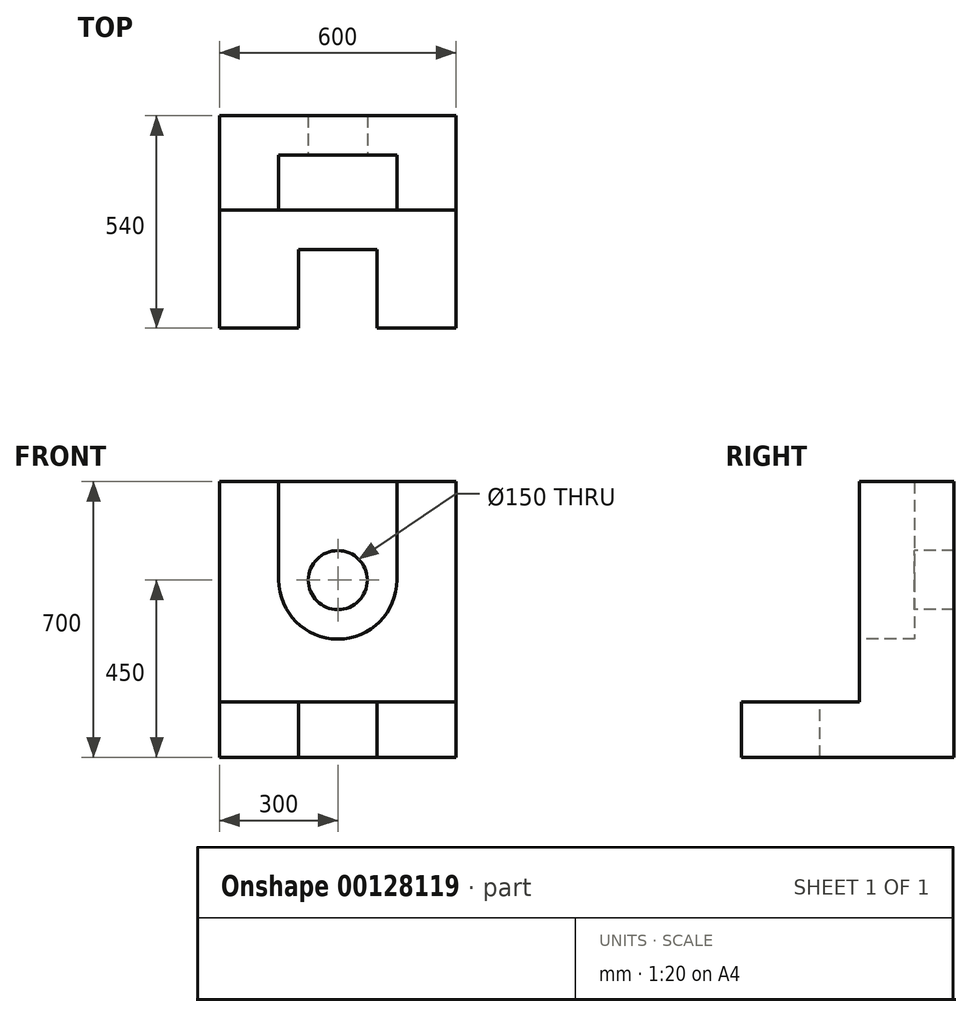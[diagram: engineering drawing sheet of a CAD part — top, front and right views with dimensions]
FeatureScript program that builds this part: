
annotation { "Feature Type Name" : "Feature", "Feature Type Description" : "" }
export const myFeature = defineFeature(function(context is Context, id is Id, definition is map)
    precondition{}
    {
        {
            var Q0;
            Q0=qCreatedBy(makeId("Top.planeOp"),FACE);
            var sketch = newSketch(context, id + "F0", { "sketchPlane" : qUnion([Q0])});
            skLineSegment(sketch, "E0.bottom", {"start": v(300, -150) * mm, "end": v(-300, -150) * mm});
            skLineSegment(sketch, "E0.top", {"start": v(300, 150) * mm, "end": v(-300, 150) * mm});
            skLineSegment(sketch, "E0.left", {"start": v(300, -150) * mm, "end": v(300, 150) * mm});
            skLineSegment(sketch, "E0.right", {"start": v(-300, -150) * mm, "end": v(-300, 150) * mm});
            skPoint(sketch, "E0.middle", {"position": v(0, 0) * mm});
            skSolve(sketch);
        }
        {
            var Q0;
            Q0 = qSketchRegion(id + "F0", true);
            extrude(context, id + "F1", {"entities" : qUnion([Q0]), "depth" : 140 * mm});
        }
        {
            var Q0;
            Q0=makeQuery(id+"F1.opExtrude","CAP_FACE",FACE,{"disambiguationData":[OSD([sQuery(id+"F0.wireOp",EDGE,"E0.bottom"),sQuery(id+"F0.wireOp",EDGE,"E0.top"),sQuery(id+"F0.wireOp",EDGE,"E0.left"),sQuery(id+"F0.wireOp",EDGE,"E0.right")])],"isStart":false});
            var sketch = newSketch(context, id + "F2", { "sketchPlane" : qUnion([Q0])});
            skLineSegment(sketch, "E1.bottom", {"start": v(100, 50) * mm, "end": v(-100, 50) * mm});
            skLineSegment(sketch, "E1.top", {"start": v(100, -350) * mm, "end": v(-100, -350) * mm});
            skLineSegment(sketch, "E1.left", {"start": v(100, 50) * mm, "end": v(100, -350) * mm});
            skLineSegment(sketch, "E1.right", {"start": v(-100, 50) * mm, "end": v(-100, -350) * mm});
            skPoint(sketch, "E1.middle", {"position": v(0, -150) * mm});
            skSolve(sketch);
        }
        {
            var Q0;
            {var subQ0=sQuery(id+"F2.wireOp",EDGE,"E1.bottom");Q0=makeQuery(id+"F2.imprint","IMPRINT",FACE,{"disambiguationData":[TD([[makeQuery(id+"F2.imprint","IMPRINT",EDGE,{"derivedFrom":subQ0}),1.0]])]});}
            extrude(context, id + "F3", {"entities" : qUnion([Q0]), "operationType" : NewBodyOperationType.REMOVE, "endBound" : BoundingType.THROUGH_ALL, "oppositeDirection" : true, "depth" : 25 * mm});
        }
        {
            var Q0;
            Q0=makeQuery(id+"F1.opExtrude","SWEPT_FACE",FACE,{"disambiguationData":[OSD([sQuery(id+"F0.wireOp",EDGE,"E0.top")])]});
            var sketch = newSketch(context, id + "F4", { "sketchPlane" : qUnion([Q0])});
            skLineSegment(sketch, "E2.bottom", {"start": v(300, 0) * mm, "end": v(-300, 0) * mm});
            skLineSegment(sketch, "E2.top", {"start": v(300, 700) * mm, "end": v(-300, 700) * mm});
            skLineSegment(sketch, "E2.left", {"start": v(300, 0) * mm, "end": v(300, 700) * mm});
            skLineSegment(sketch, "E2.right", {"start": v(-300, 0) * mm, "end": v(-300, 700) * mm});
            skSolve(sketch);
        }
        {
            var Q0;
            Q0 = qSketchRegion(id + "F4", true);
            extrude(context, id + "F5", {"entities" : qUnion([Q0]), "operationType" : NewBodyOperationType.ADD, "depth" : 240 * mm});
        }
        {
            var Q0;
            Q0=makeQuery(id+"F5.opExtrude","CAP_FACE",FACE,{"disambiguationData":[OSD([sQuery(id+"F4.wireOp",EDGE,"E2.bottom"),sQuery(id+"F4.wireOp",EDGE,"E2.top"),sQuery(id+"F4.wireOp",EDGE,"E2.left"),sQuery(id+"F4.wireOp",EDGE,"E2.right")])],"isStart":true});
            var sketch = newSketch(context, id + "F6", { "sketchPlane" : qUnion([Q0])});
            skLineSegment(sketch, "E3", {"start": v(150, 700) * mm, "end": v(150, 450) * mm});
            skLineSegment(sketch, "E4", {"start": v(-150, 450) * mm, "end": v(-150, 700) * mm});
            skLineSegment(sketch, "E5", {"start": v(-150, 700) * mm, "end": v(150, 700) * mm});
            skArc(sketch, "E6", {"start": v(-150, 450) * mm, "mid": v(0, 300) * mm, "end": v(150, 450) * mm});
            skSolve(sketch);
        }
        {
            var Q0;
            Q0=makeQuery(id+"F6.imprint","IMPRINT",FACE,{"disambiguationData":[TD([[makeQuery(id+"F6.imprint","IMPRINT",EDGE,{"derivedFrom":sQuery(id+"F6.wireOp",EDGE,"E3")}),-1.0]])]});
            extrude(context, id + "F7", {"entities" : qUnion([Q0]), "operationType" : NewBodyOperationType.REMOVE, "oppositeDirection" : true, "depth" : 140 * mm});
        }
        {
            var Q0;
            Q0=makeQuery(id+"F7.boolean.opBoolean","COPY",FACE,{"derivedFrom":makeQuery(id+"F7.opExtrude","CAP_FACE",FACE,{"disambiguationData":[OSD([sQuery(id+"F6.wireOp",EDGE,"E3"),sQuery(id+"F6.wireOp",EDGE,"E4"),sQuery(id+"F6.wireOp",EDGE,"E5"),sQuery(id+"F6.wireOp",EDGE,"E6")])],"isStart":false})});
            var sketch = newSketch(context, id + "F8", { "sketchPlane" : qUnion([Q0])});
            skCircle(sketch, "E7", {"center": v(0, 450) * mm, "radius": 75 * mm});
            skSolve(sketch);
        }
        {
            var Q0;
            Q0=makeQuery(id+"F8.imprint","IMPRINT",FACE,{"disambiguationData":[TD([[makeQuery(id+"F8.imprint","IMPRINT",EDGE,{"derivedFrom":sQuery(id+"F8.wireOp",EDGE,"E7")}),1.0]])]});
            extrude(context, id + "F9", {"entities" : qUnion([Q0]), "operationType" : NewBodyOperationType.REMOVE, "endBound" : BoundingType.THROUGH_ALL, "oppositeDirection" : true, "depth" : 25 * mm});
        }
    });
